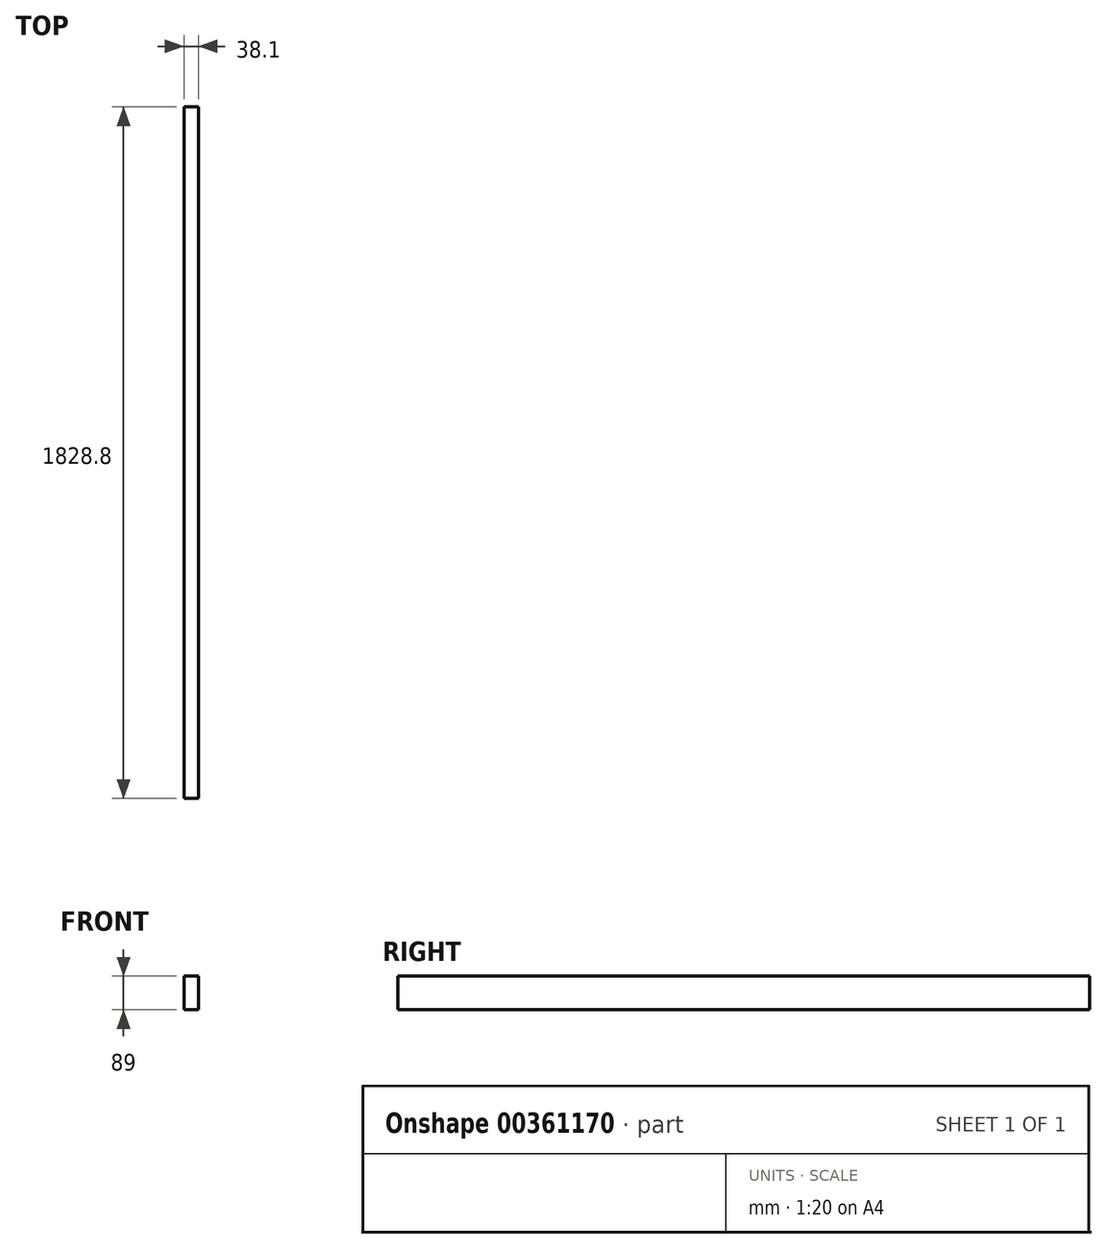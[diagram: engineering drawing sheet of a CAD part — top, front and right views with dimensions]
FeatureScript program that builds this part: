
annotation { "Feature Type Name" : "Feature", "Feature Type Description" : "" }
export const myFeature = defineFeature(function(context is Context, id is Id, definition is map)
    precondition{}
    {
        {
            var Q0;
            Q0=qCreatedBy(makeId("Front.planeOp"),FACE);
            var sketch = newSketch(context, id + "F0", { "sketchPlane" : qUnion([Q0])});
            skLineSegment(sketch, "E0.bottom", {"start": v(0, 44.5) * mm, "end": v(38.1, 44.5) * mm});
            skLineSegment(sketch, "E0.top", {"start": v(0, -44.5) * mm, "end": v(38.1, -44.5) * mm});
            skLineSegment(sketch, "E0.left", {"start": v(0, 44.5) * mm, "end": v(0, -44.5) * mm});
            skLineSegment(sketch, "E0.right", {"start": v(38.1, 44.5) * mm, "end": v(38.1, -44.5) * mm});
            skSolve(sketch);
        }
        {
            var Q0;
            Q0=makeQuery(id+"F0.imprint","IMPRINT",FACE,{"disambiguationData":[TD([[makeQuery(id+"F0.imprint","IMPRINT",EDGE,{"derivedFrom":sQuery(id+"F0.wireOp",EDGE,"E0.bottom")}),-1.0]])]});
            extrude(context, id + "F1", {"entities" : qUnion([Q0]), "endBound" : BoundingType.SYMMETRIC, "depth" : 1828.8 * mm, "offsetDistance" : 30.48 * mm});
        }
    });
